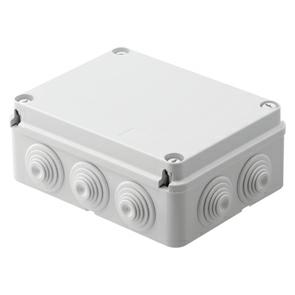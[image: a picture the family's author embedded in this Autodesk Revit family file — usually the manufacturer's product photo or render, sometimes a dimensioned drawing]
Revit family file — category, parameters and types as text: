
# Revit family: Building-SurfaceMountingEnclosures-GEWISS-44CE-JUNCTION-BOXES-WALL-MOUNTING_10HOLES
name_source: partatom
category: Apparecchi elettrici
revit_build: Autodesk Revit 2016 (Build: 20161004_0715(x64)
units: mm (PartAtom-declared; Revit-internal decimal feet)

## family parameters
Condiviso = No
Host = Superficie
Mantenere orientamento annotazione = Sì
Numero OmniClass = 23.80.30.14.24
Punto di calcolo locali = Sì
Quota connettore circolare = Usa diametro
Taglio con vuoti quando caricato = No
Tipo di parte = Normale
Titolo OmniClass = Junction Boxes

## types (1)
- Building-SurfaceMountingEnclosures-GEWISS-44CE-JUNCTION-BOXES-WALL-MOUNTING_10HOLES
    Accessories for insulation restoring = GW44621, GW44622
    Application = Special uses
    Carico apparente = 0 VA
    Catalogue = BUILDING
    Catalogue Range = 44 CE
    Classificazione = Other
    Colour = Grey RAL 7035
    Coperchio = GEWISS COPERCHIO
    Descrizione = JUNCT.BOX GL.190X140X70 IP55 GWT 960°C
    Dettaglio = elemto di dettaglio - 44CE-10IN : 190X140X70
    Diametro ingresso tubo = 15 mm  [stored 0.0492126 ft]
    Distanza fori = 33 mm
    EAN code = 8011564180345
    Electrocod = 02210
    Entries No. holes / Ã˜ = 10 / 37
    Glow Wire Test = 960°C
    IDF = 7be45fc0-f167-40fe-a13d-bceeea1662ed
    IDT = 88e3e63d-0354-4f23-ba6b-67f479272731
    IP degree = IP55
    Immagine tipo = GW44057.jpg
    Insulation class = II (according to IEC 61140 standards)
    Internal dim. LxHxD (mm) = 190x140x70
    Larghezza_interna = 190 mm  [stored 0.62336 ft]
    Lid = Plain screwed
    Lid screws (no. and type) = 4 insul. sealable hinged
    Lunghezza_interna = 140 mm  [stored 0.459318 ft]
    Material = Technopolymer GWPLAST 75
    Modello = GW44057
    Operating temperature = -25 +60 °C
    Produttore = GEWISS S.p.A.
    Prospetto di default = 1219 mm
    SEO = Box
    Scatola = GEWISS SCATOLA
    Shock resistance = IK08
    Spessore = 70 mm  [stored 0.229659 ft]
    Technical sheet = https://www.gewiss.com
    Thermo-pressure with ball = 85
    Torque screws tightening = 1,8NM
    URL = https://www.gewiss.com
    Version file RFA = 18.0
    Voltaggio_x = 0 V
    Walls = With cable glands

note: source unit labels omitted for Thermo-pressure with ball — the stored unit's dimension contradicts the parameter name (converter mislabeling)

note: [stored X ft] marks values corroborated as IEEE doubles in the binary element streams (Revit-internal decimal feet)

## geometry (parser evidence)
native form markers: Blend x2, Sweep x1
no freeform markers — native parametric forms only
